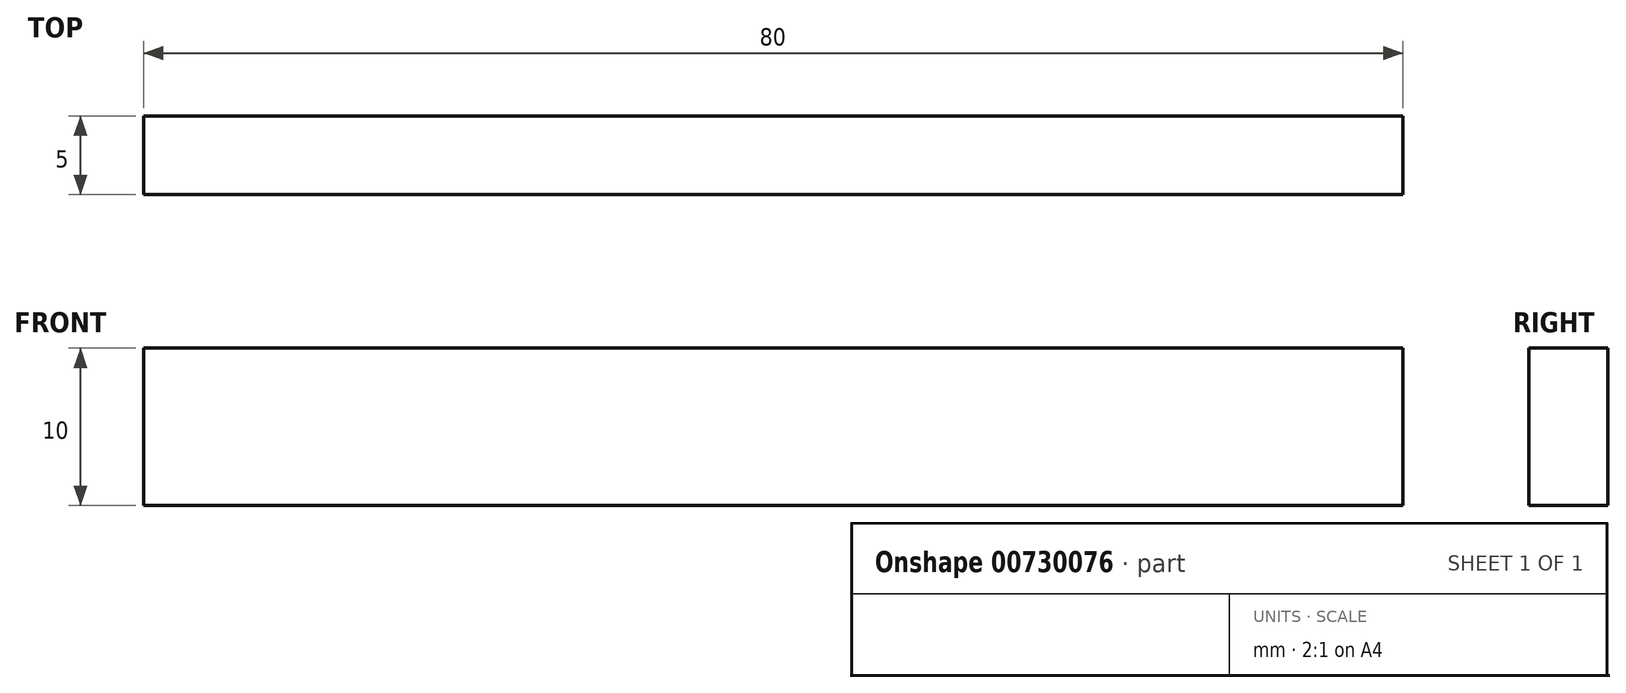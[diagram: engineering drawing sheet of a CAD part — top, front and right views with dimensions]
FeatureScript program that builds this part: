
annotation { "Feature Type Name" : "Feature", "Feature Type Description" : "" }
export const myFeature = defineFeature(function(context is Context, id is Id, definition is map)
    precondition{}
    {
        {
            var Q0;
            Q0=qCreatedBy(makeId("Front.planeOp"),FACE);
            var sketch = newSketch(context, id + "F0", { "sketchPlane" : qUnion([Q0])});
            skLineSegment(sketch, "E0.bottom", {"start": v(0, 0) * mm, "end": v(80, 0) * mm});
            skLineSegment(sketch, "E0.top", {"start": v(0, 10) * mm, "end": v(80, 10) * mm});
            skLineSegment(sketch, "E0.left", {"start": v(0, 0) * mm, "end": v(0, 10) * mm});
            skLineSegment(sketch, "E0.right", {"start": v(80, 0) * mm, "end": v(80, 10) * mm});
            skSolve(sketch);
        }
        {
            var Q0;
            Q0=makeQuery(id+"F0.imprint","IMPRINT",FACE,{"disambiguationData":[TD([[makeQuery(id+"F0.imprint","IMPRINT",EDGE,{"derivedFrom":sQuery(id+"F0.wireOp",EDGE,"E0.bottom")}),1.0]])]});
            extrude(context, id + "F1", {"entities" : qUnion([Q0]), "depth" : 5 * mm, "offsetDistance" : 25 * mm});
        }
    });
